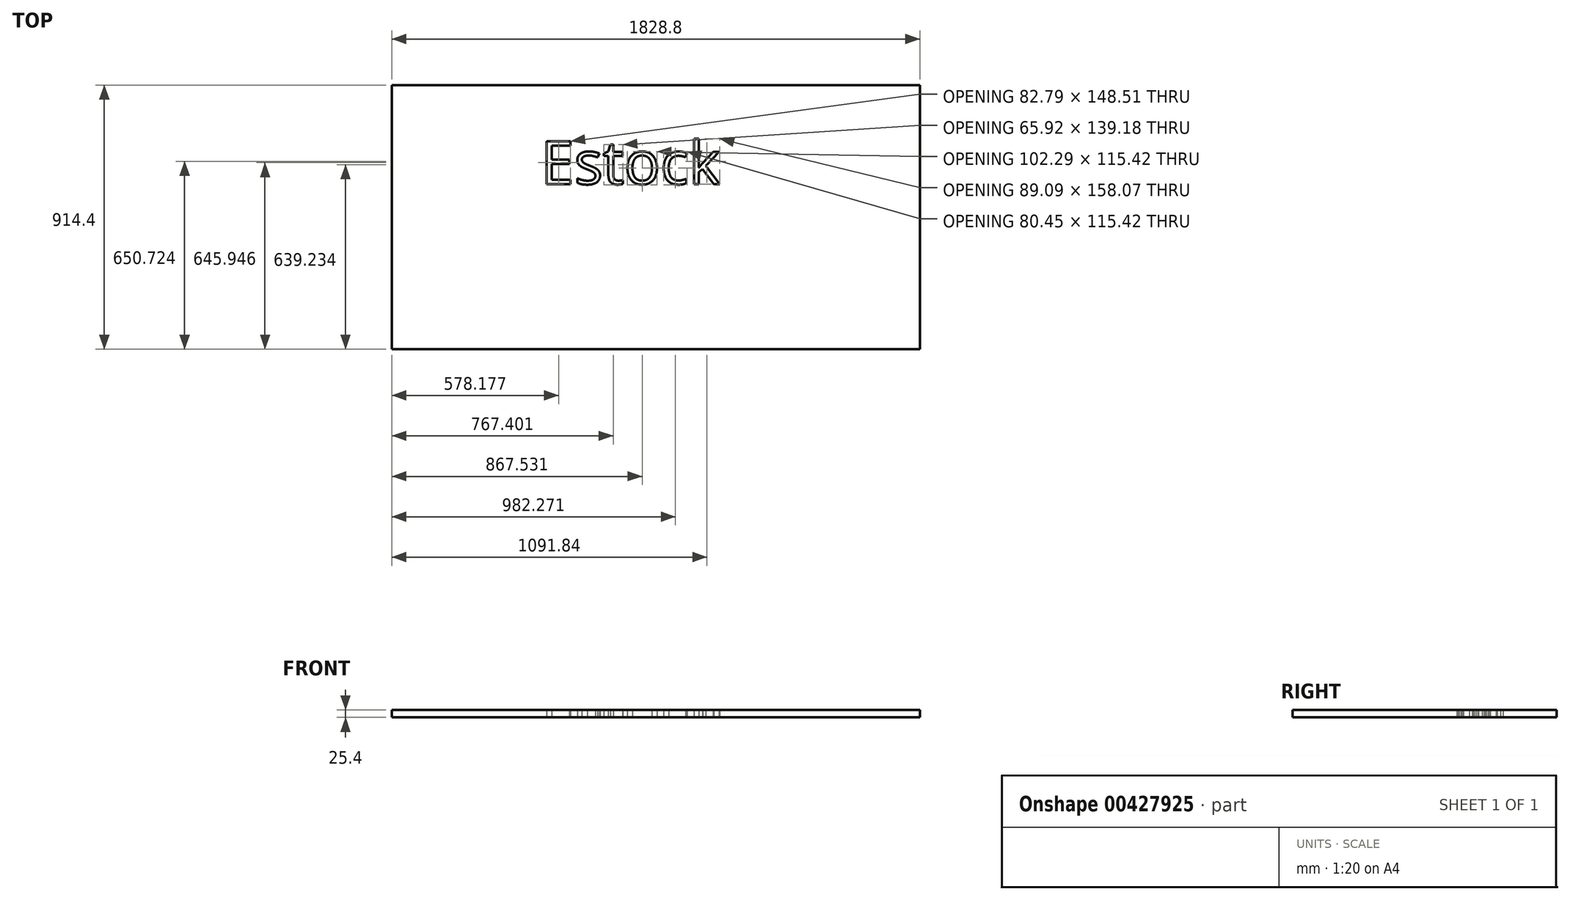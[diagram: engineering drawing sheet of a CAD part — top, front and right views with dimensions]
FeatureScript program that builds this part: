
annotation { "Feature Type Name" : "Feature", "Feature Type Description" : "" }
export const myFeature = defineFeature(function(context is Context, id is Id, definition is map)
    precondition{}
    {
        {
            var Q0;
            Q0=qCreatedBy(makeId("Top.planeOp"),FACE);
            var sketch = newSketch(context, id + "F0", { "sketchPlane" : qUnion([Q0])});
            skLineSegment(sketch, "E0.bottom", {"start": v(-61.7, -49.34) * mm, "end": v(1767.1, -49.34) * mm});
            skLineSegment(sketch, "E0.top", {"start": v(-61.7, 865.06) * mm, "end": v(1767.1, 865.06) * mm});
            skLineSegment(sketch, "E0.left", {"start": v(-61.7, -49.34) * mm, "end": v(-61.7, 865.06) * mm});
            skLineSegment(sketch, "E0.right", {"start": v(1767.1, -49.34) * mm, "end": v(1767.1, 865.06) * mm});
            skLineSegment(sketch, "E1", {"start": v(1767.1, 407.86) * mm, "end": v(1741.7, 407.86) * mm});
            skLineSegment(sketch, "E2", {"start": v(1741.7, 407.86) * mm, "end": v(1741.7, 436.43) * mm});
            skText(sketch, "E3", { "text": "Estock", "fontName": "OpenSans-Regular.ttf"});
            const initialGuessF0  = {"E3": [0.45468, 0.52235, 1, 0, 0.14978]};
            skSetInitialGuess(sketch, initialGuessF0);
            skSolve(sketch);
        }
        {
            var Q0;
            Q0 = qSketchRegion(id + "F0", true);
            var Q1;
            Q1=makeQuery(id+"F0.imprint","IMPRINT",FACE,{"disambiguationData":[TD([[makeQuery(id+"F0.imprint","IMPRINT",EDGE,{"derivedFrom":sQuery(id+"F0.wireOp",EDGE,"E3.sketch_text.stroke-65")}),1.0]])]});
            extrude(context, id + "F1", {"entities" : qUnion([Q0, Q1]), "depth" : 25.4 * mm});
        }
    });
